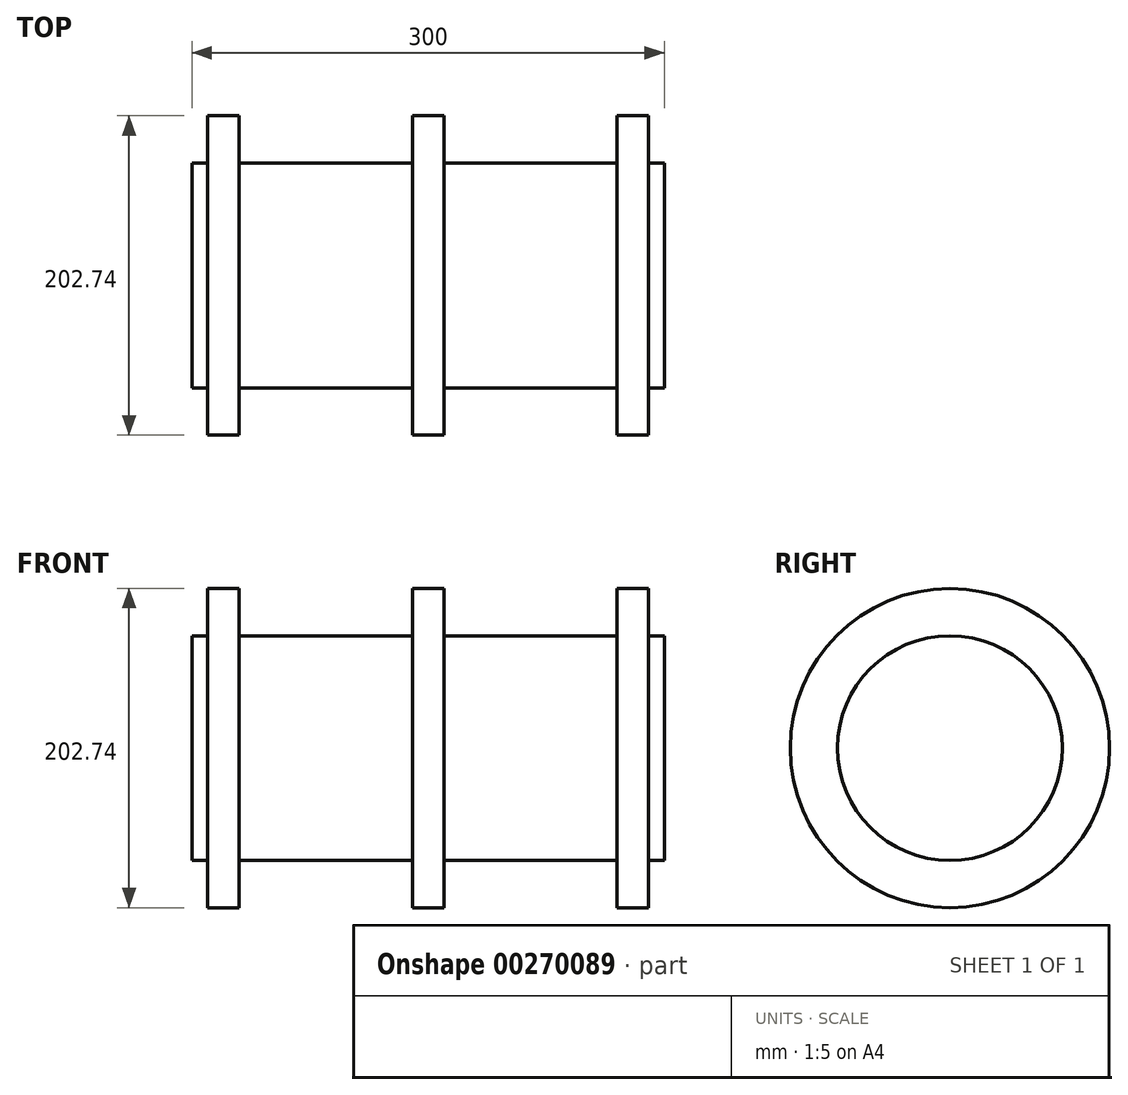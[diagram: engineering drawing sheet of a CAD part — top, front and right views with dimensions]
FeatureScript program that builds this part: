
annotation { "Feature Type Name" : "Feature", "Feature Type Description" : "" }
export const myFeature = defineFeature(function(context is Context, id is Id, definition is map)
    precondition{}
    {
        {
            var Q0;
            Q0=qCreatedBy(makeId("Top.planeOp"),FACE);
            var sketch = newSketch(context, id + "F0", { "sketchPlane" : qUnion([Q0])});
            skLineSegment(sketch, "E0", {"start": v(-150, 0) * mm, "end": v(-150, 71.37) * mm});
            skLineSegment(sketch, "E1", {"start": v(-150, 71.37) * mm, "end": v(-140, 71.37) * mm});
            skLineSegment(sketch, "E2", {"start": v(-140, 71.37) * mm, "end": v(-140, 101.37) * mm});
            skLineSegment(sketch, "E3", {"start": v(-140, 101.37) * mm, "end": v(-120, 101.37) * mm});
            skLineSegment(sketch, "E4", {"start": v(-120, 101.37) * mm, "end": v(-120, 71.37) * mm});
            skLineSegment(sketch, "E5", {"start": v(-120, 71.37) * mm, "end": v(-10, 71.37) * mm});
            skLineSegment(sketch, "E6", {"start": v(-10, 71.37) * mm, "end": v(-10, 101.37) * mm});
            skLineSegment(sketch, "E7", {"start": v(-10, 101.37) * mm, "end": v(10, 101.37) * mm});
            skLineSegment(sketch, "E8", {"start": v(10, 101.37) * mm, "end": v(10, 71.37) * mm});
            skLineSegment(sketch, "E9", {"start": v(10, 71.37) * mm, "end": v(120, 71.37) * mm});
            skLineSegment(sketch, "E10", {"start": v(120, 71.37) * mm, "end": v(120, 101.37) * mm});
            skLineSegment(sketch, "E11", {"start": v(120, 101.37) * mm, "end": v(140, 101.37) * mm});
            skLineSegment(sketch, "E12", {"start": v(140, 101.37) * mm, "end": v(140, 71.37) * mm});
            skLineSegment(sketch, "E13", {"start": v(140, 71.37) * mm, "end": v(150, 71.37) * mm});
            skLineSegment(sketch, "E14", {"start": v(150, 71.37) * mm, "end": v(150, 0) * mm});
            skLineSegment(sketch, "E15", {"start": v(150, 0) * mm, "end": v(-150, 0) * mm});
            skPoint(sketch, "E16", {"position": v(0, 101.37) * mm});
            skSolve(sketch);
        }
        {
            var Q0;
            Q0=makeQuery(id+"F0.imprint","IMPRINT",FACE,{"disambiguationData":[TD([[makeQuery(id+"F0.imprint","IMPRINT",EDGE,{"derivedFrom":sQuery(id+"F0.wireOp",EDGE,"E0")}),-1.0]])]});
            var Q1;
            Q1=sQuery(id+"F0.wireOp",EDGE,"E15");
            revolve(context, id + "F1", {"entities" : qUnion([Q0]), "axis" : qUnion([Q1]), "revolveType" : RevolveType.FULL});
        }
    });
